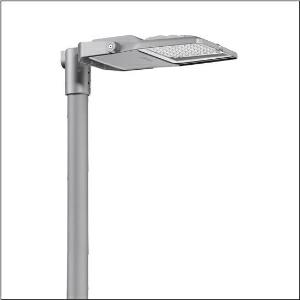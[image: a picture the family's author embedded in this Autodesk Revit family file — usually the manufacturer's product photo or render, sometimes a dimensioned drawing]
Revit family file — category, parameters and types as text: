
# Revit family: floodlight_fl_21_iq_mini___pl43_5xa7771d2a3a_a639
name_source: partatom
category: Lighting Fixtures
units: mm (PartAtom-declared; Revit-internal decimal feet)

## family parameters
Cut with Voids When Loaded = No
Host = Face
Light Source = No
Part Type = Normal
Room Calculation Point = No
Round Connector Dimension = Use Diameter
Shared = No

## types (1)
- --- (1 x LED, 18290 lm, 143 W, 3000K)
    Apparent Load = 143 VA
    CIE Flux Codes = 27 78 99 100 100
    Color Rendering = 70
    Color Temperature = 3000K
    Default Elevation = 1800 mm
    Description = Floodlight FL 21 iQ mini, floodlight, primary light control with lens, of PMMA, primary optical cover: protective disc, of toughened safety glass, transparent, light distribution: PL43, light emission: direct distribution, installation type: surface-mounted, LED, High Power LED, rated luminous flux: 18.290lm, luminous efficacy: 128lm/W, light colour: 730, colour temperature: 3000K, control: Auto-Match, Temp-Guard, Lumen-Switch, Night-Set, Smart-Wire, Light-Fading, Desk-Remote (wireless, voltage-free reading and setting of iQ features in the workshop via application-optimized NFC function/RFID function), optimised constant luminous flux control (CLO 2.0), with terminal, 6-pole, mains connection: 220..240V, AC, 50/60Hz, start of lifetime: 143W, end of service life: 152W, reduction: 61W, luminaire housing, of diecast aluminium, powder-coated, Siteco® metallic grey (DB 702S), corrosivity category C5 mid according to DIN EN ISO 12944, sealing non-destructively replaceable, please order mast flange separately, mast bracket, of steel, galvanised, powder-coated, Siteco® metallic grey (DB 702S), protection rating (complete): IP66, insulation class (complete): insulation class II (safety insulation), certification: CE, ENEC, VDE, protection symbol: D, impact resistance: IK08, permissible operating ambient temperature: -40..+40°C, permissible operating ambient temperature for outdoor applications: -40..+50°C, standard: DIN EN 12944, LABS conformity tested according to VDMA 24364:2018-05, packaging unit: 1 piece

Light Distribution: PL43
    Height = 70 mm
    Lamp = 1 x LED
    Lamp Light Flux = 18290 lm
    Lamp Power = 143 W
    Lamp count = 1
    Length = 485 mm
    Luminous efficacy = 128 lm/W
    Manufacturer = Siteco
    ModVariant = No
    Model = 5XA7771D2A3A
    Number of Poles = 1
    OnlyDefault = Yes
    Power Factor = 1
    Product Name = Floodlight FL 21 iQ mini | PL43
    Product group = floodlight | pylon annexe
    ProductGroupID = 6200
    Protection Class = Protection class II
    Protection Degree = IP 66
    RLX_Detail_Level = 1
    RLX_Emergency_Light_Flux = 0 lm
    RLX_Emergency_Type = 0
    RLX_Emergency_Type_DB = No
    RlxData = <blob elided: 101417 chars, md5=7d9ff248>
    Socket = socket
    Standby Power = 0 W
    System Light Flux = 18290 lm
    System Power = 143 W
    Type Comments = factory setting: luminous flux: 100 % | dim-lin: 254 | 730 mA
    Type Image = l_1007125.jpg
    URL = http://relux.com
    VarID = @adj_132199
    Voltage = 0 V
    Weight = 0.00 kg
    Width = 337 mm

## geometry (parser evidence)
native form markers: Blend x4, Sweep x10
no freeform markers — native parametric forms only
